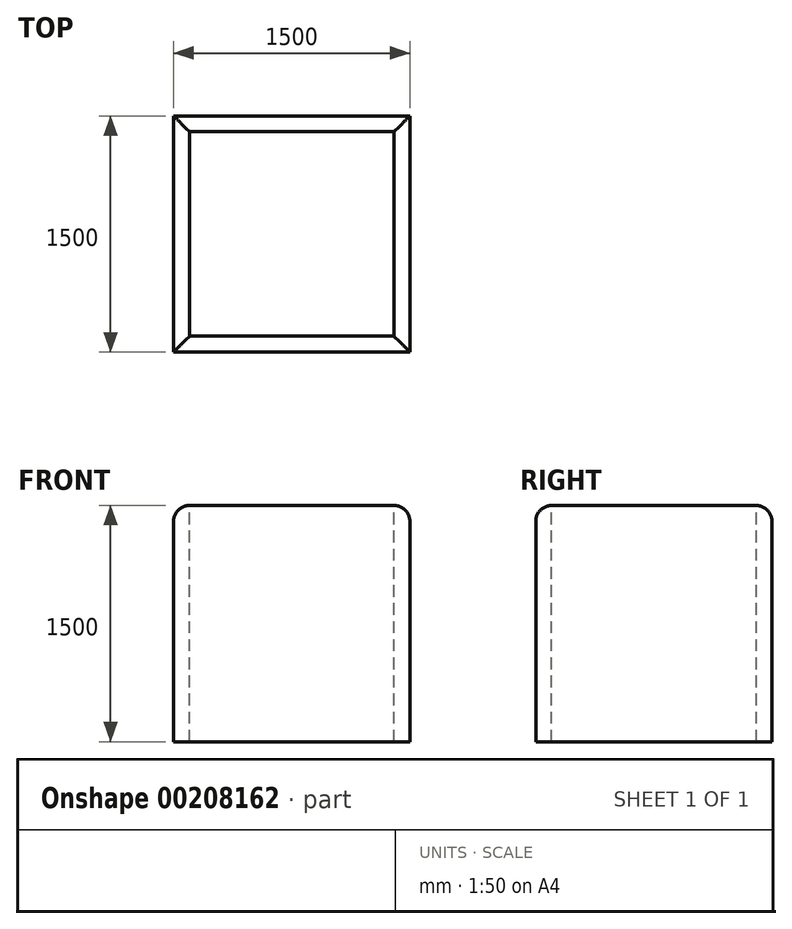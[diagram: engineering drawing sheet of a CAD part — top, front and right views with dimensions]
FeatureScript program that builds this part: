
annotation { "Feature Type Name" : "Feature", "Feature Type Description" : "" }
export const myFeature = defineFeature(function(context is Context, id is Id, definition is map)
    precondition{}
    {
        {
            var Q0;
            Q0=qCreatedBy(makeId("Top.planeOp"),FACE);
            var sketch = newSketch(context, id + "F2", { "sketchPlane" : qUnion([Q0])});
            skLineSegment(sketch, "E0.bottom", {"start": v(750, -750) * mm, "end": v(-750, -750) * mm});
            skLineSegment(sketch, "E0.top", {"start": v(750, 750) * mm, "end": v(-750, 750) * mm});
            skLineSegment(sketch, "E0.left", {"start": v(750, -750) * mm, "end": v(750, 750) * mm});
            skLineSegment(sketch, "E0.right", {"start": v(-750, -750) * mm, "end": v(-750, 750) * mm});
            skPoint(sketch, "E0.middle", {"position": v(0, 0) * mm});
            skSolve(sketch);
        }
        {
            var Q0;
            Q0 = qSketchRegion(id + "F2", true);
            extrude(context, id + "F0", {"entities" : qUnion([Q0]), "depth" : 1500 * mm});
        }
        {
            var Q0;
            Q0=makeQuery(id+"F0.opExtrude","CAP_FACE",FACE,{"disambiguationData":[OSD([sQuery(id+"F2.wireOp",EDGE,"E0.bottom"),sQuery(id+"F2.wireOp",EDGE,"E0.top"),sQuery(id+"F2.wireOp",EDGE,"E0.left"),sQuery(id+"F2.wireOp",EDGE,"E0.right")])],"isStart":false});
            fillet(context, id + "F1", {"entities" : qUnion([Q0]), "radius" : 100 * mm, "tangentPropagation" : true, "allowEdgeOverflow" : false});
        }
        {
            var Q0;
            Q0=makeQuery(id+"F0.opExtrude","CAP_FACE",FACE,{"disambiguationData":[OSD([sQuery(id+"F2.wireOp",EDGE,"E0.bottom"),sQuery(id+"F2.wireOp",EDGE,"E0.top"),sQuery(id+"F2.wireOp",EDGE,"E0.left"),sQuery(id+"F2.wireOp",EDGE,"E0.right")])],"isStart":false});
            var sketch = newSketch(context, id + "F3", { "sketchPlane" : qUnion([Q0])});
            skLineSegment(sketch, "E1.bottom", {"start": v(142, -142) * mm, "end": v(-142, -142) * mm});
            skLineSegment(sketch, "E1.top", {"start": v(142, 142) * mm, "end": v(-142, 142) * mm});
            skLineSegment(sketch, "E1.left", {"start": v(142, -142) * mm, "end": v(142, 142) * mm});
            skLineSegment(sketch, "E1.right", {"start": v(-142, -142) * mm, "end": v(-142, 142) * mm});
            skPoint(sketch, "E1.middle", {"position": v(0, 0) * mm});
            skSolve(sketch);
        }
        {
            var Q0;
            Q0=makeQuery(id+"F3.imprint","IMPRINT",FACE,{"disambiguationData":[TD([[makeQuery(id+"F3.imprint","IMPRINT",EDGE,{"derivedFrom":sQuery(id+"F3.wireOp",EDGE,"E1.bottom")}),-1.0]])]});
            var Q1;
            Q1=makeQuery(id+"F3.imprint","IMPRINT",FACE,{"disambiguationData":[TD([[makeQuery(id+"F3.imprint","IMPRINT",EDGE,{"derivedFrom":sQuery(id+"F3.wireOp",EDGE,"E1.bottom")}),1.0]])]});
            extrude(context, id + "F4", {"entities" : qUnion([Q0, Q1]), "operationType" : NewBodyOperationType.REMOVE, "oppositeDirection" : true, "depth" : 1500 * mm});
        }
    });
